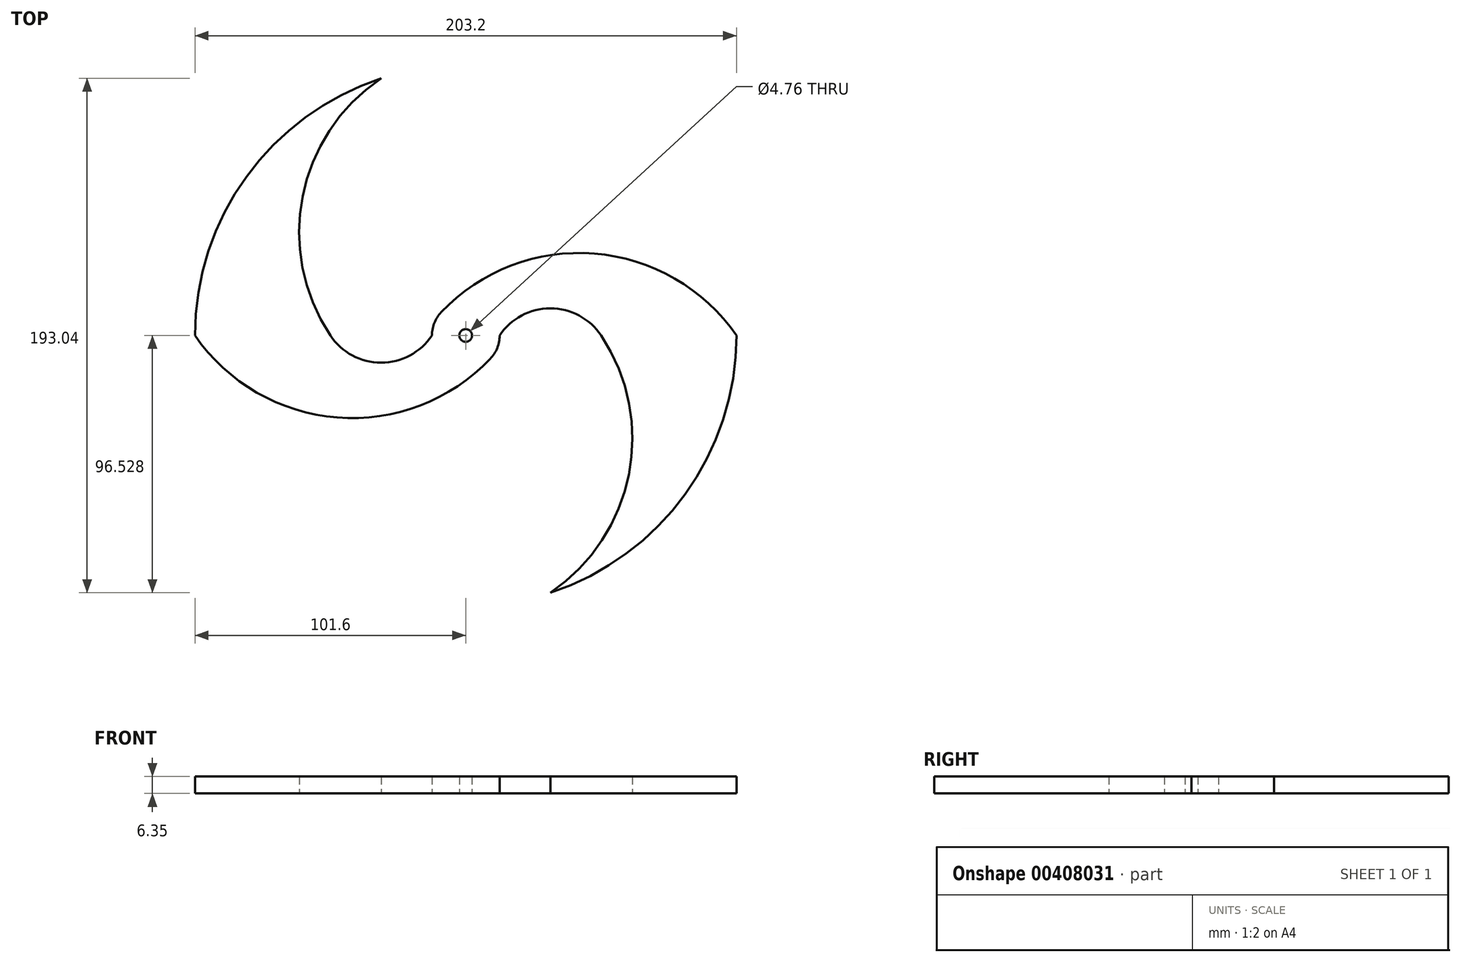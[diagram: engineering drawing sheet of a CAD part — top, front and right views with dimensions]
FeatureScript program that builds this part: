
annotation { "Feature Type Name" : "Feature", "Feature Type Description" : "" }
export const myFeature = defineFeature(function(context is Context, id is Id, definition is map)
    precondition{}
    {
        {
            var Q0;
            Q0=qCreatedBy(makeId("Top.planeOp"),FACE);
            var sketch = newSketch(context, id + "F0", { "sketchPlane" : qUnion([Q0])});
            skArc(sketch, "E0", {"start": v(-9.2, 8.76) * mm, "mid": v(-11.8, 4.72) * mm, "end": v(-12.7, 0) * mm});
            skArc(sketch, "E1", {"start": v(101.6, 0) * mm, "mid": v(48.29, 30.74) * mm, "end": v(-9.2, 8.76) * mm});
            skCircle(sketch, "E2", {"center": v(0, 0) * mm, "radius": 105 * mm, "construction": true});
            skArc(sketch, "E3", {"start": v(50.8, 0) * mm, "mid": v(31.75, 10.2) * mm, "end": v(12.7, 0) * mm});
            skArc(sketch, "E4", {"start": v(50.8, 0) * mm, "mid": v(61.2, -52.2) * mm, "end": v(31.75, -96.52) * mm});
            skArc(sketch, "E5.MirrorCS", {"start": v(-50.8, 0) * mm, "mid": v(-31.75, -10.2) * mm, "end": v(-12.7, 0) * mm});
            skArc(sketch, "E6.MirrorCS", {"start": v(-50.8, 0) * mm, "mid": v(-61.2, 52.2) * mm, "end": v(-31.75, 96.52) * mm});
            skArc(sketch, "E7", {"start": v(31.75, -96.52) * mm, "mid": v(82.3, -59.57) * mm, "end": v(101.6, 0) * mm});
            skArc(sketch, "E8", {"start": v(-101.6, 0) * mm, "mid": v(-48.29, -30.75) * mm, "end": v(9.2, -8.76) * mm});
            skArc(sketch, "E9", {"start": v(-31.75, 96.52) * mm, "mid": v(-82.3, 59.57) * mm, "end": v(-101.6, 0) * mm});
            skArc(sketch, "E10.trimOffspring", {"start": v(9.2, -8.76) * mm, "mid": v(11.8, -4.72) * mm, "end": v(12.7, 0) * mm});
            skCircle(sketch, "E11", {"center": v(0, 0) * mm, "radius": 2.38 * mm});
            skSolve(sketch);
        }
        {
            var Q0;
            Q0 = qSketchRegion(id + "F0", true);
            extrude(context, id + "F1", {"entities" : qUnion([Q0]), "depth" : 6.35 * mm, "offsetDistance" : 25.4 * mm});
        }
    });
